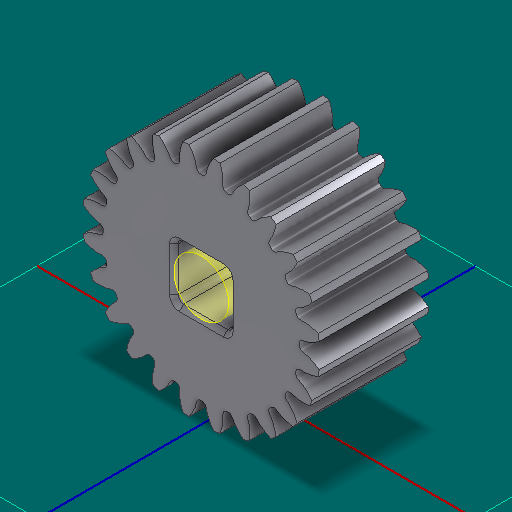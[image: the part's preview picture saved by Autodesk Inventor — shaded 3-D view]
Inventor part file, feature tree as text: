
AUTODESK INVENTOR PART (.ipt)
format: ipt  version: 2025 (Build 290162000, 162)  size: 477,696 bytes
history: native  units: in
note: dims shown in document units (in); Inventor stores cm internally (conversion verified against a paired STEP export)
features: other x5, sketch x1
ambient origin geometry x8: Origin, YZ Plane, XZ Plane, XY Plane, X Axis, Y Axis, Z Axis, Center Point
bodies: Solid1 (feature_tree)
feature tree (6):
  other  "HS 24T Gear, No Insert_mirrored.ipt"
  other  "Solid1::HS 24T Gear, No Insert_mirrored.ipt"
  other  "TaggingFeature1"
  sketch  "Sketch1"  dims[d0=0.3937in]
  other  "Srf1"
  other  "Srf1::Derived"
